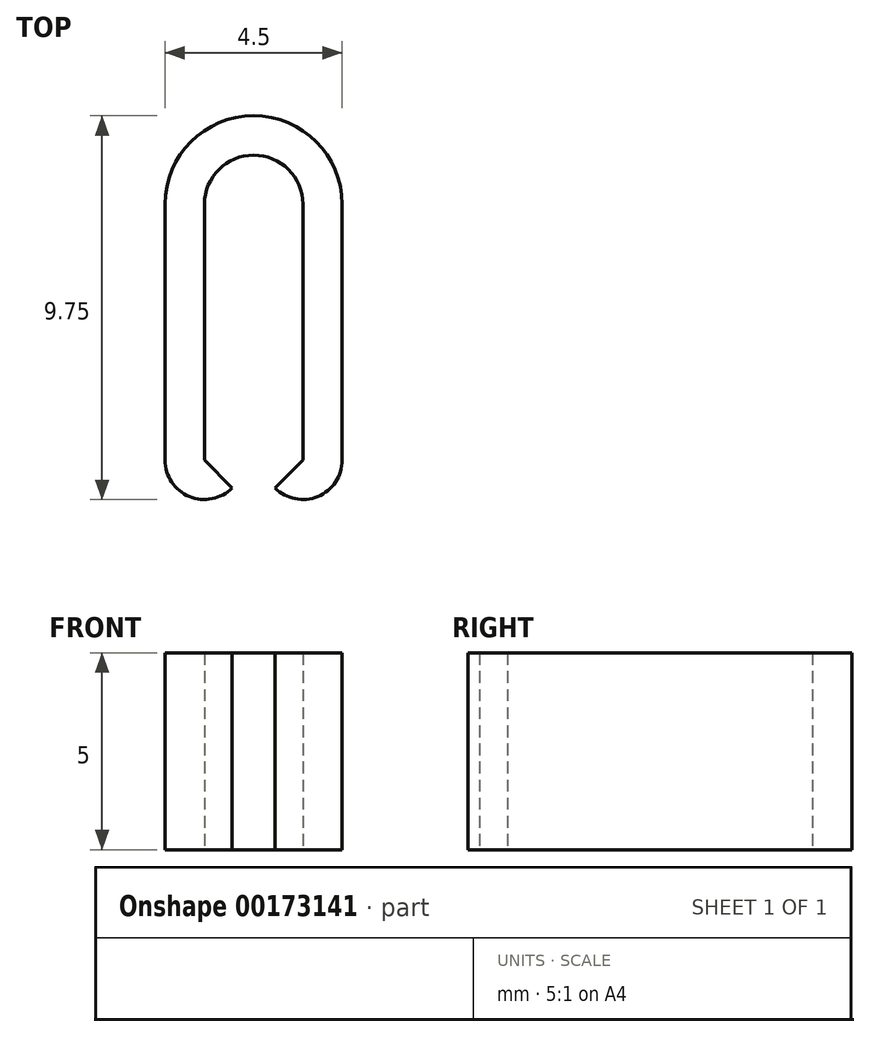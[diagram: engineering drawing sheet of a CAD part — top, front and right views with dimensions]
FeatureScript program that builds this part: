
annotation { "Feature Type Name" : "Feature", "Feature Type Description" : "" }
export const myFeature = defineFeature(function(context is Context, id is Id, definition is map)
    precondition{}
    {
        {
            var Q0;
            Q0=qCreatedBy(makeId("Top.planeOp"),FACE);
            var sketch = newSketch(context, id + "F0", { "sketchPlane" : qUnion([Q0])});
            skLineSegment(sketch, "E0.bottom", {"start": v(1.25, 0) * mm, "end": v(2.25, 0) * mm});
            skLineSegment(sketch, "E0.top", {"start": v(1.25, -6.5) * mm, "end": v(2.25, -6.5) * mm});
            skLineSegment(sketch, "E0.left", {"start": v(1.25, 0) * mm, "end": v(1.25, -6.5) * mm});
            skLineSegment(sketch, "E0.right", {"start": v(2.25, 0) * mm, "end": v(2.25, -6.5) * mm});
            skLineSegment(sketch, "E1.bottom", {"start": v(-1.25, 0) * mm, "end": v(-2.25, 0) * mm});
            skLineSegment(sketch, "E1.top", {"start": v(-1.25, -6.5) * mm, "end": v(-2.25, -6.5) * mm});
            skLineSegment(sketch, "E1.left", {"start": v(-1.25, 0) * mm, "end": v(-1.25, -6.5) * mm});
            skLineSegment(sketch, "E1.right", {"start": v(-2.25, 0) * mm, "end": v(-2.25, -6.5) * mm});
            skPoint(sketch, "E2", {"position": v(0, 0) * mm});
            skArc(sketch, "E3", {"start": v(2.25, 0) * mm, "mid": v(0, 2.25) * mm, "end": v(-2.25, 0) * mm});
            skArc(sketch, "E4", {"start": v(1.25, 0) * mm, "mid": v(0, 1.25) * mm, "end": v(-1.25, 0) * mm});
            skArc(sketch, "E5", {"start": v(-2.25, -6.5) * mm, "mid": v(-1.63, -7.42) * mm, "end": v(-0.54, -7.2) * mm});
            skLineSegment(sketch, "E6", {"start": v(-1.25, -6.5) * mm, "end": v(-0.54, -7.2) * mm});
            skPoint(sketch, "E7.orphan", {"position": v(-7.75, 0) * mm});
            skLineSegment(sketch, "E8", {"start": v(-1.25, 6.05) * mm, "end": v(1.25, 6.05) * mm});
            skLineSegment(sketch, "E9.MirrorCS", {"start": v(1.25, -6.5) * mm, "end": v(0.54, -7.2) * mm});
            skArc(sketch, "E10.MirrorCS", {"start": v(2.25, -6.5) * mm, "mid": v(1.63, -7.42) * mm, "end": v(0.54, -7.2) * mm});
            skSolve(sketch);
        }
        {
            var Q0;
            Q0 = qSketchRegion(id + "F0", true);
            extrude(context, id + "F1", {"entities" : qUnion([Q0]), "depth" : 5 * mm});
        }
    });
